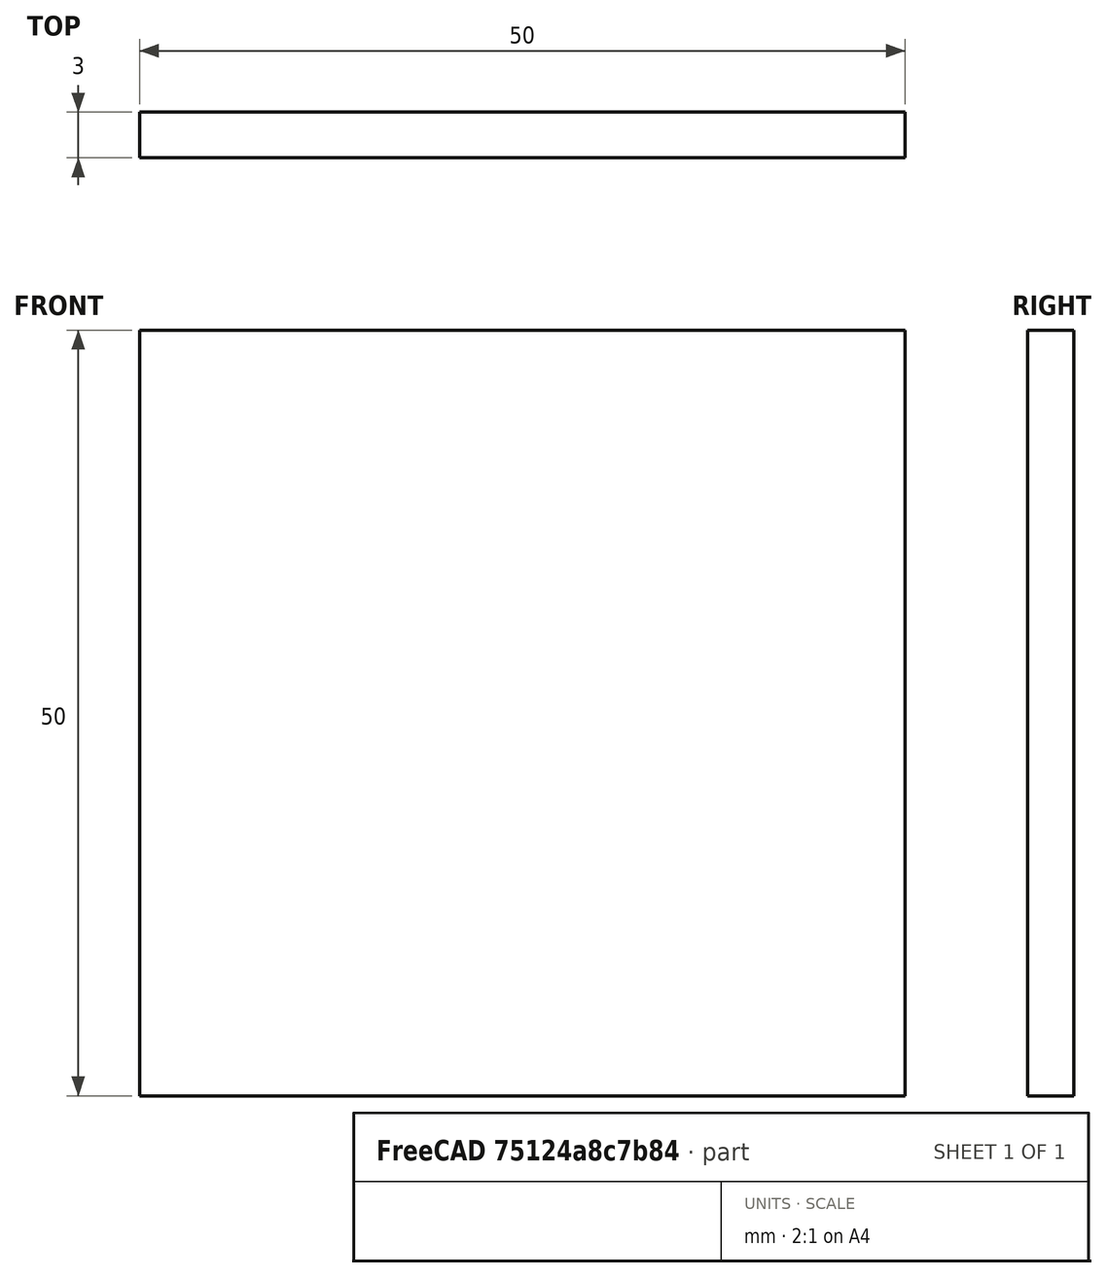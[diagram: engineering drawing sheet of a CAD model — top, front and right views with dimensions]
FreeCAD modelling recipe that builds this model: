
FCSTD DOCUMENT  (FreeCAD 0.15R4671 (Git))
Label: Flat Bar 50x3 EN10058 S235JR
License: All rights reserved
LicenseURL: http://en.wikipedia.org/wiki/All_rights_reserved
objects: Sketcher::SketchObject×1, Part::Extrusion×1
note: 2 computed .brp shape members not serialized (recipe doc carries the construction recipe); baked Part::Feature solids carry a one-line shape summary decoded from their .brp

FEATURE [Sketcher::SketchObject] Sketch
  sketch-geometry (4):
    g0: LineSegment StartX=-25 StartY=-1.5 StartZ=0 EndX=25 EndY=-1.5 EndZ=0
    g1: LineSegment StartX=25 StartY=-1.5 StartZ=0 EndX=25 EndY=1.5 EndZ=0
    g2: LineSegment StartX=25 StartY=1.5 StartZ=0 EndX=-25 EndY=1.5 EndZ=0
    g3: LineSegment StartX=-25 StartY=1.5 StartZ=0 EndX=-25 EndY=-1.5 EndZ=0
  constraints (12):
    c: Coincident(g0,g1)
    c: Coincident(g1,g2)
    c: Coincident(g2,g3)
    c: Coincident(g3,g0)
    c: Horizontal(g0)
    c: Horizontal(g2)
    c: Vertical(g1)
    c: Vertical(g3)
    c: Symmetric(g1,g2,g-2)
    c: Symmetric(g0,g1,g-1)
    c: DistanceY(g1) = 3
    c: DistanceX(g0) = 50
FEATURE [Part::Extrusion] Extrude  label="Flat Bar 50x3 EN10058 S235JR"
  Base = -> Sketch
  Dir = (0,0,50)
  Solid = true
